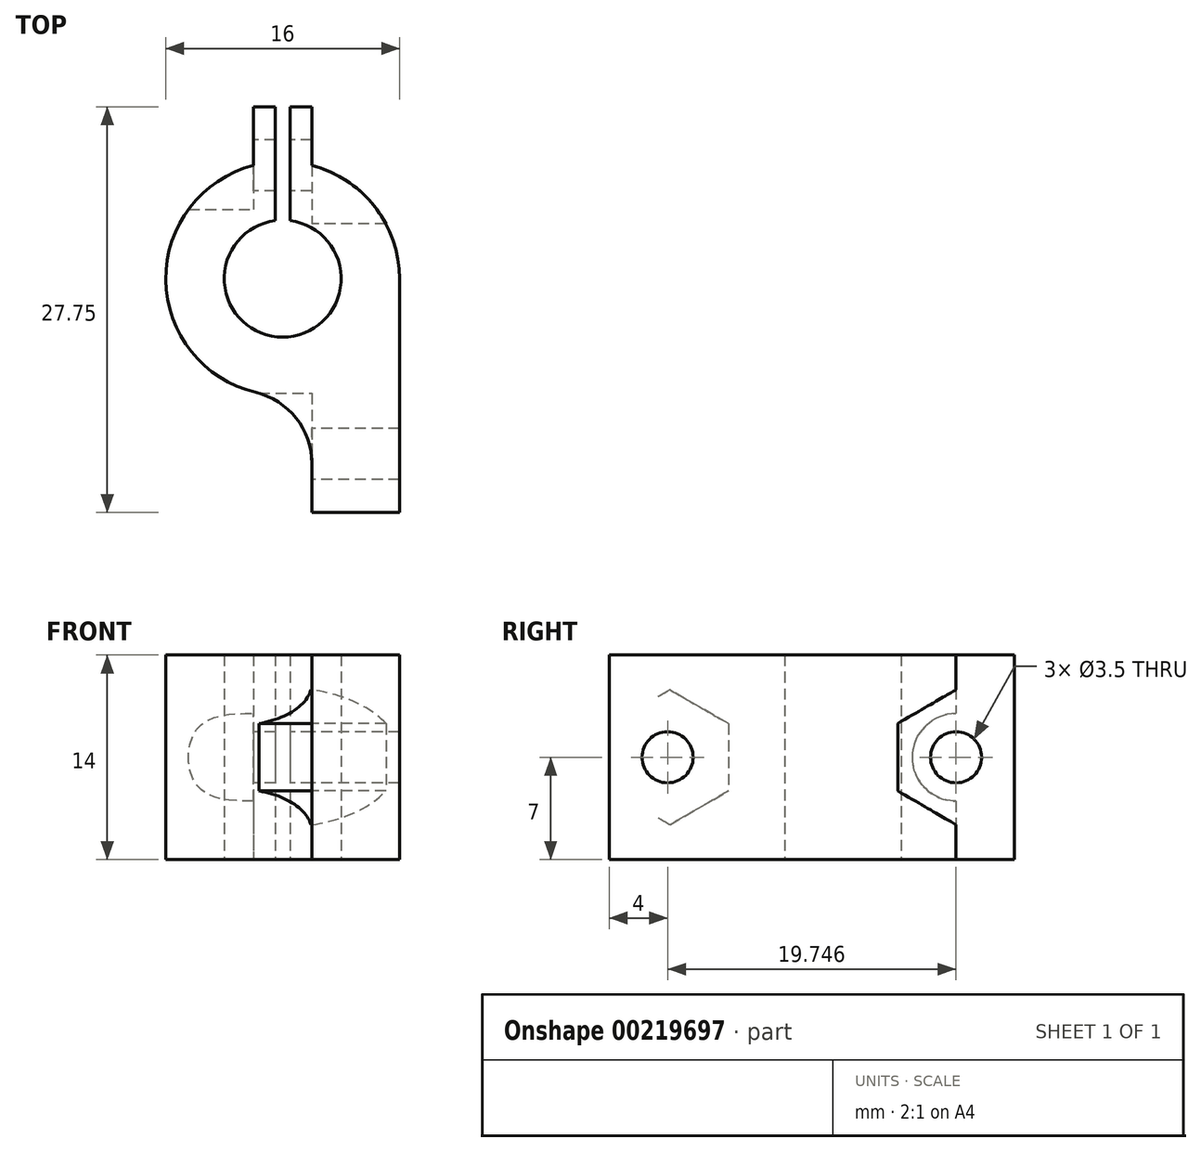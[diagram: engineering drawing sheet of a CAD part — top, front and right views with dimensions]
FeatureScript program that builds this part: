
annotation { "Feature Type Name" : "Feature", "Feature Type Description" : "" }
export const myFeature = defineFeature(function(context is Context, id is Id, definition is map)
    precondition{}
    {
        {
            var Q0;
            Q0=qCreatedBy(makeId("Top.planeOp"),FACE);
            var sketch = newSketch(context, id + "F0", { "sketchPlane" : qUnion([Q0])});
            skArc(sketch, "E0", {"start": v(0.5, 3.97) * mm, "mid": v(0, -4) * mm, "end": v(-0.5, 3.97) * mm});
            skLineSegment(sketch, "E1", {"start": v(-0.5, 3.97) * mm, "end": v(0.5, 3.97) * mm, "construction": true});
            skLineSegment(sketch, "E2", {"start": v(-0.5, 3.97) * mm, "end": v(-0.5, 11.75) * mm});
            skLineSegment(sketch, "E3", {"start": v(-0.5, 11.75) * mm, "end": v(-2, 11.75) * mm});
            skLineSegment(sketch, "E4", {"start": v(-2, 11.75) * mm, "end": v(-2, 7.75) * mm});
            skLineSegment(sketch, "E5", {"start": v(0.5, 3.97) * mm, "end": v(0.5, 11.75) * mm});
            skLineSegment(sketch, "E6", {"start": v(0.5, 11.75) * mm, "end": v(2, 11.75) * mm});
            skLineSegment(sketch, "E7", {"start": v(2, 11.75) * mm, "end": v(2, 7.75) * mm});
            skArc(sketch, "E8", {"start": v(2, 7.75) * mm, "mid": v(0, -8) * mm, "end": v(-2, 7.75) * mm, "construction": true});
            skLineSegment(sketch, "E9", {"start": v(8, 0) * mm, "end": v(8, -16) * mm});
            skLineSegment(sketch, "E10", {"start": v(8, -16) * mm, "end": v(2, -16) * mm});
            skLineSegment(sketch, "E11", {"start": v(2, -16) * mm, "end": v(2, -12.65) * mm});
            skArc(sketch, "E12", {"start": v(2, 7.75) * mm, "mid": v(6.32, 4.9) * mm, "end": v(8, 0) * mm});
            skArc(sketch, "E13", {"start": v(-1.85, -7.78) * mm, "mid": v(-8, -0.08) * mm, "end": v(-2, 7.75) * mm});
            skPoint(sketch, "E14.visualSharp", {"position": v(2, -7.75) * mm});
            skArc(sketch, "E14.filletArc", {"start": v(2, -12.65) * mm, "mid": v(0.92, -9.55) * mm, "end": v(-1.85, -7.78) * mm});
            skLineSegment(sketch, "E15", {"start": v(0, -8) * mm, "end": v(8, -8) * mm, "construction": true});
            skSolve(sketch);
        }
        {
            var Q0;
            Q0 = qSketchRegion(id + "F0", true);
            extrude(context, id + "F1", {"entities" : qUnion([Q0]), "depth" : 14 * mm});
        }
        {
            var Q0;
            Q0=makeQuery(id+"F1.opExtrude","SWEPT_FACE",FACE,{"disambiguationData":[OSD([sQuery(id+"F0.wireOp",EDGE,"E4")])]});
            var sketch = newSketch(context, id + "F2", { "sketchPlane" : qUnion([Q0])});
            skCircle(sketch, "E16", {"center": v(-7.75, 7) * mm, "radius": 3 * mm});
            skSolve(sketch);
        }
        {
            var Q0;
            Q0 = qSketchRegion(id + "F2", true);
            extrude(context, id + "F3", {"entities" : qUnion([Q0]), "operationType" : NewBodyOperationType.REMOVE, "endBound" : BoundingType.THROUGH_ALL, "depth" : 25 * mm});
        }
        {
            var Q0;
            Q0=makeQuery(id+"F3.boolean.opBoolean","MERGE",FACE,{"derivedFrom":[makeQuery(id+"F1.opExtrude","SWEPT_FACE",FACE,{"disambiguationData":[OSD([sQuery(id+"F0.wireOp",EDGE,"E4")])]}),makeQuery(id+"F3.opExtrude","CAP_FACE",FACE,{"disambiguationData":[OSD([sQuery(id+"F2.wireOp",EDGE,"E16")])],"isStart":true})]});
            var sketch = newSketch(context, id + "F4", { "sketchPlane" : qUnion([Q0])});
            skCircle(sketch, "E17", {"center": v(-7.75, 7) * mm, "radius": 1.75 * mm});
            skSolve(sketch);
        }
        {
            var Q0;
            Q0 = qSketchRegion(id + "F4", true);
            extrude(context, id + "F5", {"entities" : qUnion([Q0]), "operationType" : NewBodyOperationType.REMOVE, "endBound" : BoundingType.THROUGH_ALL, "oppositeDirection" : true, "depth" : 25 * mm});
        }
        {
            var Q0;
            Q0=makeQuery(id+"F1.opExtrude","SWEPT_FACE",FACE,{"disambiguationData":[OSD([sQuery(id+"F0.wireOp",EDGE,"E7")])]});
            var sketch = newSketch(context, id + "F6", { "sketchPlane" : qUnion([Q0])});
            skCircle(sketch, "E18.cCircle", {"center": v(7.75, 7) * mm, "radius": 4 * mm, "construction": true});
            skLineSegment(sketch, "E18.0", {"start": v(7.75, 2.38) * mm, "end": v(3.75, 4.7) * mm});
            skLineSegment(sketch, "E18.1", {"start": v(3.75, 4.7) * mm, "end": v(3.75, 9.3) * mm});
            skLineSegment(sketch, "E18.2", {"start": v(3.75, 9.3) * mm, "end": v(7.75, 11.62) * mm});
            skLineSegment(sketch, "E18.3", {"start": v(7.75, 11.62) * mm, "end": v(11.75, 9.3) * mm});
            skLineSegment(sketch, "E18.4", {"start": v(11.75, 9.3) * mm, "end": v(11.75, 4.7) * mm});
            skLineSegment(sketch, "E18.5", {"start": v(11.75, 4.7) * mm, "end": v(7.75, 2.38) * mm});
            skPoint(sketch, "E18.0.midPoint", {"position": v(5.75, 3.54) * mm});
            skSolve(sketch);
        }
        {
            var Q0;
            Q0 = qSketchRegion(id + "F6", true);
            extrude(context, id + "F7", {"entities" : qUnion([Q0]), "operationType" : NewBodyOperationType.REMOVE, "endBound" : BoundingType.THROUGH_ALL, "depth" : 25 * mm});
        }
        {
            var Q0;
            Q0=makeQuery(id+"F1.opExtrude","SWEPT_FACE",FACE,{"disambiguationData":[OSD([sQuery(id+"F0.wireOp",EDGE,"E11")])]});
            var sketch = newSketch(context, id + "F8", { "sketchPlane" : qUnion([Q0])});
            skCircle(sketch, "E19", {"center": v(12, 7) * mm, "radius": 1.75 * mm});
            skPoint(sketch, "E19.centerSnap0", {"position": v(12.65, 7) * mm});
            skSolve(sketch);
        }
        {
            var Q0;
            Q0 = qSketchRegion(id + "F8", true);
            extrude(context, id + "F9", {"entities" : qUnion([Q0]), "operationType" : NewBodyOperationType.REMOVE, "endBound" : BoundingType.THROUGH_ALL, "oppositeDirection" : true, "depth" : 25 * mm});
        }
        {
            var Q0;
            Q0=makeQuery(id+"F1.opExtrude","SWEPT_FACE",FACE,{"disambiguationData":[OSD([sQuery(id+"F0.wireOp",EDGE,"E11")])]});
            var sketch = newSketch(context, id + "F10", { "sketchPlane" : qUnion([Q0])});
            skLineSegment(sketch, "E20", {"start": v(16, 7) * mm, "end": v(0, 7) * mm, "construction": true});
            skCircle(sketch, "E21.cCircle", {"center": v(11.84, 7) * mm, "radius": 4 * mm, "construction": true});
            skLineSegment(sketch, "E21.0", {"start": v(11.84, 11.62) * mm, "end": v(15.84, 9.3) * mm});
            skLineSegment(sketch, "E21.1", {"start": v(15.84, 9.3) * mm, "end": v(15.84, 4.7) * mm});
            skLineSegment(sketch, "E21.2", {"start": v(15.84, 4.7) * mm, "end": v(11.84, 2.38) * mm});
            skLineSegment(sketch, "E21.3", {"start": v(11.84, 2.38) * mm, "end": v(7.84, 4.7) * mm});
            skLineSegment(sketch, "E21.4", {"start": v(7.84, 4.7) * mm, "end": v(7.84, 9.3) * mm});
            skLineSegment(sketch, "E21.5", {"start": v(7.84, 9.3) * mm, "end": v(11.84, 11.62) * mm});
            skPoint(sketch, "E21.0.midPoint", {"position": v(13.84, 10.46) * mm});
            skSolve(sketch);
        }
        {
            var Q0;
            Q0 = qSketchRegion(id + "F10", true);
            var Q1;
            Q1 = qConstructionFilter(qBodyType(qCreatedBy(id + "F10" ,EDGE), BodyType.WIRE), ConstructionObject.NO);
            extrude(context, id + "F11", {"entities" : qUnion([Q0]), "operationType" : NewBodyOperationType.REMOVE, "surfaceEntities" : qUnion([Q1]), "endBound" : BoundingType.THROUGH_ALL, "depth" : 25 * mm});
        }
    });
